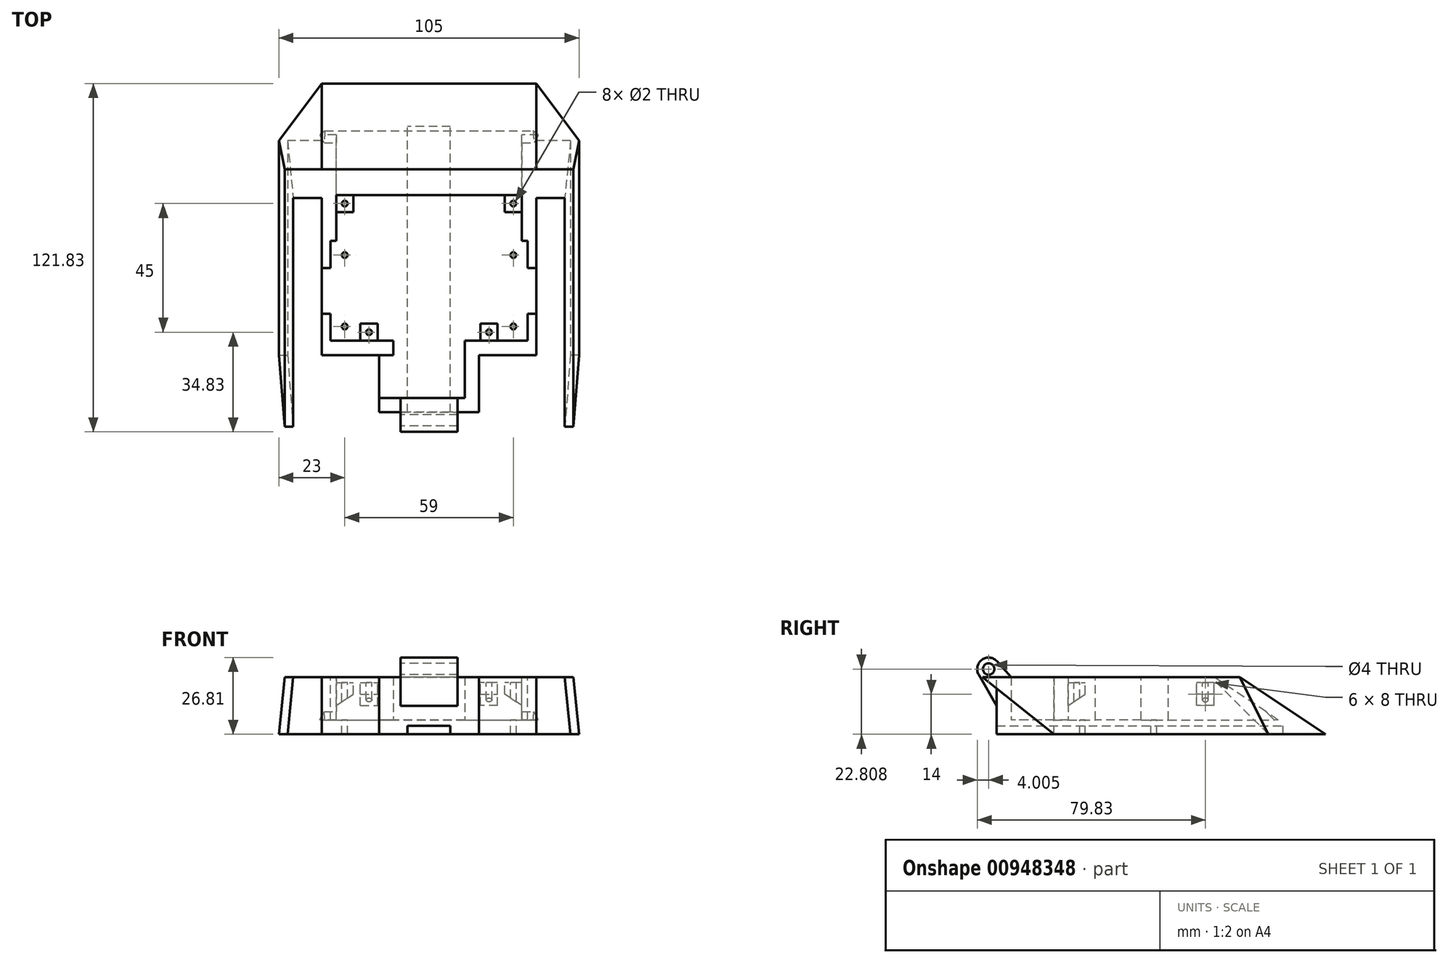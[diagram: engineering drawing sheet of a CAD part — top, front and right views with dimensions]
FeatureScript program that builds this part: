
annotation { "Feature Type Name" : "Feature", "Feature Type Description" : "" }
export const myFeature = defineFeature(function(context is Context, id is Id, definition is map)
    precondition{}
    {
        {
            var Q0;
            Q0=qCreatedBy(makeId("Top.planeOp"),FACE);
            var sketch = newSketch(context, id + "F0", { "sketchPlane" : qUnion([Q0])});
            skLineSegment(sketch, "E0.bottom", {"start": v(-37.5, -37.5) * mm, "end": v(37.5, -37.5) * mm});
            skLineSegment(sketch, "E0.top", {"start": v(-37.5, 37.5) * mm, "end": v(37.5, 37.5) * mm, "construction": true});
            skLineSegment(sketch, "E0.left", {"start": v(-37.5, -37.5) * mm, "end": v(-37.5, 37.5) * mm});
            skLineSegment(sketch, "E0.right", {"start": v(37.5, -37.5) * mm, "end": v(37.5, 37.5) * mm});
            skPoint(sketch, "E0.middle", {"position": v(0, 0) * mm});
            skLineSegment(sketch, "E1", {"start": v(-37.5, 37.5) * mm, "end": v(-49.5, 37.5) * mm});
            skLineSegment(sketch, "E2", {"start": v(-52.5, 37.5) * mm, "end": v(-37.5, 57.5) * mm});
            skLineSegment(sketch, "E3", {"start": v(-37.5, 57.5) * mm, "end": v(37.5, 57.5) * mm});
            skLineSegment(sketch, "E4", {"start": v(37.5, 57.5) * mm, "end": v(52.5, 37.5) * mm});
            skLineSegment(sketch, "E5", {"start": v(52.5, 37.5) * mm, "end": v(37.5, 37.5) * mm});
            skLineSegment(sketch, "E6.bottom", {"start": v(-52.5, 37.5) * mm, "end": v(-49.5, 37.5) * mm, "construction": true});
            skLineSegment(sketch, "E6.top", {"start": v(-52.5, -37.5) * mm, "end": v(-49.5, -37.5) * mm});
            skLineSegment(sketch, "E6.left", {"start": v(-52.5, 37.5) * mm, "end": v(-52.5, 21.64) * mm});
            skLineSegment(sketch, "E7.bottom", {"start": v(52.5, 37.5) * mm, "end": v(49.5, 37.5) * mm, "construction": true});
            skLineSegment(sketch, "E7.top", {"start": v(52.5, -37.5) * mm, "end": v(49.5, -37.5) * mm});
            skLineSegment(sketch, "E7.left", {"start": v(52.5, 37.5) * mm, "end": v(52.5, 21.33) * mm});
            skLineSegment(sketch, "E8", {"start": v(-52.5, 21.64) * mm, "end": v(-52.5, -37.5) * mm});
            skLineSegment(sketch, "E9", {"start": v(52.5, 21.33) * mm, "end": v(52.5, -37.5) * mm});
            skLineSegment(sketch, "E10", {"start": v(-49.5, 37.5) * mm, "end": v(-49.5, -37.5) * mm});
            skLineSegment(sketch, "E11", {"start": v(49.5, 37.5) * mm, "end": v(49.5, -37.5) * mm});
            skLineSegment(sketch, "E12", {"start": v(17.5, -37.5) * mm, "end": v(17.5, -57.5) * mm});
            skLineSegment(sketch, "E13", {"start": v(17.5, -57.5) * mm, "end": v(-17.5, -57.5) * mm});
            skLineSegment(sketch, "E14", {"start": v(-17.5, -57.5) * mm, "end": v(-17.5, -37.5) * mm});
            skSolve(sketch);
        }
        {
            var Q0;
            Q0=makeQuery(id+"F0.imprint","IMPRINT",FACE,{"disambiguationData":[TD([[makeQuery(id+"F0.imprint","IMPRINT",EDGE,{"derivedFrom":sQuery(id+"F0.wireOp",EDGE,"E0.bottom")}),1.0]])]});
            cPlane(context, id + "F1", {"entities" : qUnion([Q0]), "cplaneType" : CPlaneType.OFFSET, "offset" : 20 * mm, "width" : 150 * mm, "height" : 150 * mm});
        }
        {
            var Q0;
            Q0=qCreatedBy(id+"F1.planeOp",FACE);
            var sketch = newSketch(context, id + "F2", { "sketchPlane" : qUnion([Q0])});
            skLineSegment(sketch, "E15.bottom", {"start": v(-37.5, 27.5) * mm, "end": v(37.5, 27.5) * mm});
            skLineSegment(sketch, "E15.top", {"start": v(-37.5, -37.5) * mm, "end": v(37.5, -37.5) * mm});
            skLineSegment(sketch, "E15.left", {"start": v(-37.5, 17.5) * mm, "end": v(-37.5, -37.5) * mm});
            skLineSegment(sketch, "E15.right", {"start": v(37.5, 17.5) * mm, "end": v(37.5, -37.5) * mm});
            skPoint(sketch, "E15.middle", {"position": v(0, -5) * mm});
            skLineSegment(sketch, "E16.bottom", {"start": v(-37.5, 27.5) * mm, "end": v(-50.5, 27.5) * mm});
            skLineSegment(sketch, "E16.top", {"start": v(-37.5, 17.5) * mm, "end": v(-47.5, 17.5) * mm});
            skLineSegment(sketch, "E16.right", {"start": v(-50.5, 27.5) * mm, "end": v(-50.5, 17.5) * mm});
            skLineSegment(sketch, "E17.bottom", {"start": v(37.5, 27.5) * mm, "end": v(50.5, 27.5) * mm});
            skLineSegment(sketch, "E17.top", {"start": v(37.5, 17.5) * mm, "end": v(47.5, 17.5) * mm});
            skLineSegment(sketch, "E17.right", {"start": v(50.5, 27.5) * mm, "end": v(50.5, 17.5) * mm});
            skLineSegment(sketch, "E18.top", {"start": v(-50.5, -62.5) * mm, "end": v(-47.5, -62.5) * mm});
            skLineSegment(sketch, "E18.left", {"start": v(-50.5, 17.5) * mm, "end": v(-50.5, -62.5) * mm});
            skLineSegment(sketch, "E18.right", {"start": v(-47.5, 17.5) * mm, "end": v(-47.5, -62.5) * mm});
            skLineSegment(sketch, "E19.top", {"start": v(50.5, -62.5) * mm, "end": v(47.5, -62.5) * mm});
            skLineSegment(sketch, "E19.left", {"start": v(50.5, 17.5) * mm, "end": v(50.5, -62.5) * mm});
            skLineSegment(sketch, "E19.right", {"start": v(47.5, 17.5) * mm, "end": v(47.5, -62.5) * mm});
            skLineSegment(sketch, "E20", {"start": v(17.5, -37.5) * mm, "end": v(17.5, -57.5) * mm});
            skLineSegment(sketch, "E21", {"start": v(17.5, -57.5) * mm, "end": v(-17.5, -57.5) * mm});
            skLineSegment(sketch, "E22", {"start": v(-17.5, -57.5) * mm, "end": v(-17.5, -37.5) * mm});
            skSolve(sketch);
        }
        {
            var Q0;
            Q0 = qSketchRegion(id + "F0", true);
            var Q1;
            Q1 = qSketchRegion(id + "F2", true);
            loft(context, id + "F3", {"sheetProfilesArray" : [{ "sheetProfileEntities" : qUnion([Q0]) }, { "sheetProfileEntities" : qUnion([Q1]) }]});
        }
        {
            var Q0;
            Q0=makeQuery(id+"F3.opLoft","CAP_FACE",FACE,{"disambiguationData":[OSD([makeQuery(id+"F2.imprint","IMPRINT",FACE,{"disambiguationData":[TD([[makeQuery(id+"F2.imprint","IMPRINT",EDGE,{"derivedFrom":sQuery(id+"F2.wireOp",EDGE,"E15.bottom")}),-1.0]])]})])],"isStart":true});
            shell(context, id + "F4", {"entities" : qUnion([Q0]), "thickness" : 5 * mm});
        }
        {
            var Q0;
            Q0=makeQuery(id+"F3.opLoft","CAP_FACE",FACE,{"disambiguationData":[OSD([makeQuery(id+"F2.imprint","IMPRINT",FACE,{"disambiguationData":[TD([[makeQuery(id+"F2.imprint","IMPRINT",EDGE,{"derivedFrom":sQuery(id+"F2.wireOp",EDGE,"E15.bottom")}),-1.0]])]})])],"isStart":true});
            var sketch = newSketch(context, id + "F5", { "sketchPlane" : qUnion([Q0])});
            skLineSegment(sketch, "E23", {"start": v(-32.5, -32.5) * mm, "end": v(-34.5, -32.5) * mm});
            skLineSegment(sketch, "E24", {"start": v(-34.5, -32.5) * mm, "end": v(-34.5, -23) * mm});
            skLineSegment(sketch, "E25", {"start": v(-34.5, -23) * mm, "end": v(-37.5, -23) * mm});
            skLineSegment(sketch, "E26", {"start": v(-37.5, -23) * mm, "end": v(-37.5, -7) * mm});
            skLineSegment(sketch, "E27", {"start": v(-37.5, -7) * mm, "end": v(-34.5, -7) * mm});
            skLineSegment(sketch, "E28", {"start": v(-34.5, -7) * mm, "end": v(-34.5, 2.5) * mm});
            skLineSegment(sketch, "E29", {"start": v(-34.5, 2.5) * mm, "end": v(-32.5, 2.5) * mm});
            skLineSegment(sketch, "E30", {"start": v(32.5, -32.5) * mm, "end": v(32.5, -32.5) * mm});
            skLineSegment(sketch, "E31", {"start": v(32.5, -32.5) * mm, "end": v(34.5, -32.5) * mm});
            skLineSegment(sketch, "E32", {"start": v(34.5, -32.5) * mm, "end": v(34.5, -23) * mm});
            skLineSegment(sketch, "E33", {"start": v(34.5, -23) * mm, "end": v(37.5, -23) * mm});
            skLineSegment(sketch, "E34", {"start": v(37.5, -23) * mm, "end": v(37.5, -7) * mm});
            skLineSegment(sketch, "E35", {"start": v(37.5, -7) * mm, "end": v(34.5, -7) * mm});
            skLineSegment(sketch, "E36", {"start": v(34.5, -7) * mm, "end": v(34.5, 2.5) * mm});
            skLineSegment(sketch, "E37", {"start": v(34.5, 2.5) * mm, "end": v(32.5, 2.5) * mm});
            skSolve(sketch);
        }
        {
            var Q0;
            {var subQ0=sQuery(id+"F5.wireOp",EDGE,"E31");Q0=makeQuery(id+"F5.imprint","IMPRINT",FACE,{"disambiguationData":[TD([[makeQuery(id+"F5.imprint","IMPRINT",EDGE,{"derivedFrom":subQ0}),1.0]])]});}
            var Q1;
            {var subQ0=sQuery(id+"F5.wireOp",EDGE,"E23");Q1=makeQuery(id+"F5.imprint","IMPRINT",FACE,{"disambiguationData":[TD([[makeQuery(id+"F5.imprint","IMPRINT",EDGE,{"derivedFrom":subQ0}),-1.0]])]});}
            extrude(context, id + "F6", {"entities" : qUnion([Q0, Q1]), "operationType" : NewBodyOperationType.REMOVE, "oppositeDirection" : true, "depth" : 15 * mm, "offsetDistance" : 25 * mm});
        }
        {
            var Q0;
            {var subQ0=sQuery(id+"F2.wireOp",EDGE,"E15.top");Q0=makeQuery(id+"F6.boolean.opBoolean","MERGE",FACE,{"derivedFrom":[makeQuery(id+"F4.opShell","OFFSET_FACE",FACE,{"disambiguationData":[OSD([makeQuery(id+"F0.imprint","IMPRINT",FACE,{"disambiguationData":[TD([[makeQuery(id+"F0.imprint","IMPRINT",EDGE,{"derivedFrom":sQuery(id+"F0.wireOp",EDGE,"E0.bottom")}),1.0]])]}),makeQuery(id+"F0.imprint","IMPRINT",FACE,{"disambiguationData":[TD([[makeQuery(id+"F0.imprint","IMPRINT",EDGE,{"derivedFrom":sQuery(id+"F0.wireOp",EDGE,"E7.top")}),-1.0]])]})])]})],"fromTools":[makeQuery(id+"F6.opExtrude","CAP_FACE",FACE,{"disambiguationData":[OSD([subQ0,sQuery(id+"F2.wireOp",EDGE,"E15.left"),sQuery(id+"F2.wireOp",EDGE,"E16.top"),sQuery(id+"F5.wireOp",EDGE,"E23"),sQuery(id+"F5.wireOp",EDGE,"E24"),sQuery(id+"F5.wireOp",EDGE,"E25"),sQuery(id+"F5.wireOp",EDGE,"E26"),sQuery(id+"F5.wireOp",EDGE,"E27"),sQuery(id+"F5.wireOp",EDGE,"E28"),sQuery(id+"F5.wireOp",EDGE,"E29")])],"isStart":false}),makeQuery(id+"F6.opExtrude","CAP_FACE",FACE,{"disambiguationData":[OSD([subQ0,sQuery(id+"F2.wireOp",EDGE,"E15.right"),sQuery(id+"F2.wireOp",EDGE,"E17.top"),sQuery(id+"F5.wireOp",EDGE,"E31"),sQuery(id+"F5.wireOp",EDGE,"E32"),sQuery(id+"F5.wireOp",EDGE,"E33"),sQuery(id+"F5.wireOp",EDGE,"E34"),sQuery(id+"F5.wireOp",EDGE,"E35"),sQuery(id+"F5.wireOp",EDGE,"E36"),sQuery(id+"F5.wireOp",EDGE,"E37")])],"isStart":false})]});}
            var sketch = newSketch(context, id + "F7", { "sketchPlane" : qUnion([Q0])});
            skCircle(sketch, "E38", {"center": v(-29.5, -27.5) * mm, "radius": 1 * mm});
            skCircle(sketch, "E39", {"center": v(-29.5, -2.5) * mm, "radius": 1 * mm});
            skCircle(sketch, "E40", {"center": v(29.5, -27.5) * mm, "radius": 1 * mm});
            skCircle(sketch, "E41", {"center": v(29.5, -2.5) * mm, "radius": 1 * mm});
            skSolve(sketch);
        }
        {
            var Q0;
            Q0=makeQuery(id+"F7.imprint","IMPRINT",FACE,{"disambiguationData":[TD([[makeQuery(id+"F7.imprint","IMPRINT",EDGE,{"derivedFrom":sQuery(id+"F7.wireOp",EDGE,"E38")}),1.0]])]});
            var Q1;
            Q1=makeQuery(id+"F7.imprint","IMPRINT",FACE,{"disambiguationData":[TD([[makeQuery(id+"F7.imprint","IMPRINT",EDGE,{"derivedFrom":sQuery(id+"F7.wireOp",EDGE,"E41")}),1.0]])]});
            var Q2;
            Q2=makeQuery(id+"F7.imprint","IMPRINT",FACE,{"disambiguationData":[TD([[makeQuery(id+"F7.imprint","IMPRINT",EDGE,{"derivedFrom":sQuery(id+"F7.wireOp",EDGE,"E40")}),1.0]])]});
            var Q3;
            Q3=makeQuery(id+"F7.imprint","IMPRINT",FACE,{"disambiguationData":[TD([[makeQuery(id+"F7.imprint","IMPRINT",EDGE,{"derivedFrom":sQuery(id+"F7.wireOp",EDGE,"E39")}),1.0]])]});
            extrude(context, id + "F8", {"entities" : qUnion([Q0, Q1, Q2, Q3]), "operationType" : NewBodyOperationType.REMOVE, "oppositeDirection" : true, "depth" : 25 * mm, "offsetDistance" : 25 * mm});
        }
        {
            var Q0;
            {var subQ15=sQuery(id+"F2.wireOp",EDGE,"E15.bottom");Q0=makeQuery(id+"F6.boolean.opBoolean","SPLIT",FACE,{"disambiguationData":[TD([makeQuery(id+"F6.opExtrude","SWEPT_FACE",FACE,{"disambiguationData":[OSD([sQuery(id+"F5.wireOp",EDGE,"E27")])]})])],"derivedFrom":makeQuery(id+"F3.opLoft","CAP_FACE",FACE,{"disambiguationData":[OSD([makeQuery(id+"F2.imprint","IMPRINT",FACE,{"disambiguationData":[TD([[makeQuery(id+"F2.imprint","IMPRINT",EDGE,{"derivedFrom":subQ15}),-1.0]])]})])],"isStart":true})});}
            cPlane(context, id + "F9", {"entities" : qUnion([Q0]), "cplaneType" : CPlaneType.OFFSET, "offset" : 2 * mm, "oppositeDirection" : true, "width" : 150 * mm, "height" : 150 * mm});
        }
        {
            var Q0;
            Q0=qCreatedBy(id+"F9.planeOp",FACE);
            var sketch = newSketch(context, id + "F10", { "sketchPlane" : qUnion([Q0])});
            skLineSegment(sketch, "E42.bottom", {"start": v(32.5, 18.5) * mm, "end": v(26.5, 18.5) * mm});
            skLineSegment(sketch, "E42.top", {"start": v(32.5, 12.5) * mm, "end": v(26.5, 12.5) * mm});
            skLineSegment(sketch, "E42.left", {"start": v(32.5, 18.5) * mm, "end": v(32.5, 12.5) * mm});
            skLineSegment(sketch, "E42.right", {"start": v(26.5, 18.5) * mm, "end": v(26.5, 12.5) * mm});
            skCircle(sketch, "E43", {"center": v(29.5, 15.5) * mm, "radius": 1 * mm});
            skPoint(sketch, "E43.centerSnap0", {"position": v(29.5, 12.5) * mm});
            skPoint(sketch, "E43.centerSnap1", {"position": v(26.5, 15.5) * mm});
            skLineSegment(sketch, "E44.bottom", {"start": v(24, -32.5) * mm, "end": v(18, -32.5) * mm});
            skLineSegment(sketch, "E44.top", {"start": v(24, -26.5) * mm, "end": v(18, -26.5) * mm});
            skLineSegment(sketch, "E44.left", {"start": v(24, -32.5) * mm, "end": v(24, -26.5) * mm});
            skLineSegment(sketch, "E44.right", {"start": v(18, -32.5) * mm, "end": v(18, -26.5) * mm});
            skCircle(sketch, "E45", {"center": v(21, -29.5) * mm, "radius": 1 * mm});
            skPoint(sketch, "E45.centerSnap0", {"position": v(21, -26.5) * mm});
            skPoint(sketch, "E45.centerSnap1", {"position": v(18, -29.5) * mm});
            skLineSegment(sketch, "E46", {"start": v(0, 0) * mm, "end": v(0, -25.62) * mm});
            skLineSegment(sketch, "E47.MirrorCS", {"start": v(-24, -32.5) * mm, "end": v(-24, -26.5) * mm});
            skLineSegment(sketch, "E48.MirrorCS", {"start": v(-24, -26.5) * mm, "end": v(-18, -26.5) * mm});
            skLineSegment(sketch, "E49.MirrorCS", {"start": v(-18, -32.5) * mm, "end": v(-18, -26.5) * mm});
            skLineSegment(sketch, "E50.MirrorCS", {"start": v(-24, -32.5) * mm, "end": v(-18, -32.5) * mm});
            skCircle(sketch, "E51.MirrorC", {"center": v(-21, -29.5) * mm, "radius": 1 * mm});
            skLineSegment(sketch, "E52.MirrorCS", {"start": v(-32.5, 12.5) * mm, "end": v(-26.5, 12.5) * mm});
            skLineSegment(sketch, "E53.MirrorCS", {"start": v(-32.5, 18.5) * mm, "end": v(-32.5, 12.5) * mm});
            skLineSegment(sketch, "E54.MirrorCS", {"start": v(-32.5, 18.5) * mm, "end": v(-26.5, 18.5) * mm});
            skLineSegment(sketch, "E55.MirrorCS", {"start": v(-26.5, 18.5) * mm, "end": v(-26.5, 12.5) * mm});
            skCircle(sketch, "E56.MirrorC", {"center": v(-29.5, 15.5) * mm, "radius": 1 * mm});
            skSolve(sketch);
        }
        {
            var Q0;
            Q0=makeQuery(id+"F10.imprint","IMPRINT",FACE,{"disambiguationData":[TD([[makeQuery(id+"F10.imprint","IMPRINT",EDGE,{"derivedFrom":sQuery(id+"F10.wireOp",EDGE,"E47.MirrorCS")}),-1.0]])]});
            var Q1;
            Q1=makeQuery(id+"F10.imprint","IMPRINT",FACE,{"disambiguationData":[TD([[makeQuery(id+"F10.imprint","IMPRINT",EDGE,{"derivedFrom":sQuery(id+"F10.wireOp",EDGE,"E52.MirrorCS")}),1.0]])]});
            var Q2;
            Q2=makeQuery(id+"F10.imprint","IMPRINT",FACE,{"disambiguationData":[TD([[makeQuery(id+"F10.imprint","IMPRINT",EDGE,{"derivedFrom":sQuery(id+"F10.wireOp",EDGE,"E42.bottom")}),1.0]])]});
            var Q3;
            Q3=makeQuery(id+"F10.imprint","IMPRINT",FACE,{"disambiguationData":[TD([[makeQuery(id+"F10.imprint","IMPRINT",EDGE,{"derivedFrom":sQuery(id+"F10.wireOp",EDGE,"E44.bottom")}),-1.0]])]});
            extrude(context, id + "F11", {"entities" : qUnion([Q0, Q1, Q2, Q3]), "operationType" : NewBodyOperationType.ADD, "oppositeDirection" : true, "depth" : 8 * mm, "offsetDistance" : 25 * mm});
        }
        {
            var Q0;
            Q0=makeQuery(id+"F11.opExtrude","SWEPT_FACE",FACE,{"disambiguationData":[OSD([sQuery(id+"F10.wireOp",EDGE,"E42.top")])]});
            var sketch = newSketch(context, id + "F12", { "sketchPlane" : qUnion([Q0])});
            skLineSegment(sketch, "E57", {"start": v(32.5, 10) * mm, "end": v(26.5, 14) * mm});
            skSolve(sketch);
        }
        {
            var Q0;
            {var subQ0=sQuery(id+"F12.wireOp",EDGE,"E57");Q0=makeQuery(id+"F12.imprint","IMPRINT",FACE,{"disambiguationData":[TD([[makeQuery(id+"F12.imprint","IMPRINT",EDGE,{"derivedFrom":subQ0}),1.0]])]});}
            extrude(context, id + "F13", {"entities" : qUnion([Q0]), "operationType" : NewBodyOperationType.REMOVE, "oppositeDirection" : true, "depth" : 7 * mm, "offsetDistance" : 25 * mm});
        }
        {
            var Q0;
            Q0=makeQuery(id+"F11.opExtrude","SWEPT_FACE",FACE,{"disambiguationData":[OSD([sQuery(id+"F10.wireOp",EDGE,"E52.MirrorCS")])]});
            var sketch = newSketch(context, id + "F14", { "sketchPlane" : qUnion([Q0])});
            skLineSegment(sketch, "E58", {"start": v(-32.5, 10) * mm, "end": v(-26.5, 14) * mm});
            skSolve(sketch);
        }
        {
            var Q0;
            {var subQ0=sQuery(id+"F14.wireOp",EDGE,"E58");Q0=makeQuery(id+"F14.imprint","IMPRINT",FACE,{"disambiguationData":[TD([[makeQuery(id+"F14.imprint","IMPRINT",EDGE,{"derivedFrom":subQ0}),-1.0]])]});}
            extrude(context, id + "F15", {"entities" : qUnion([Q0]), "operationType" : NewBodyOperationType.REMOVE, "oppositeDirection" : true, "depth" : 7 * mm, "offsetDistance" : 25 * mm});
        }
        {
            var Q0;
            Q0=makeQuery(id+"F11.opExtrude","SWEPT_FACE",FACE,{"disambiguationData":[OSD([sQuery(id+"F10.wireOp",EDGE,"E44.left")])]});
            var sketch = newSketch(context, id + "F16", { "sketchPlane" : qUnion([Q0])});
            skLineSegment(sketch, "E59", {"start": v(-32.5, 10) * mm, "end": v(-26.5, 14) * mm});
            skSolve(sketch);
        }
        {
            var Q0;
            {var subQ0=sQuery(id+"F16.wireOp",EDGE,"E59");Q0=makeQuery(id+"F16.imprint","IMPRINT",FACE,{"disambiguationData":[TD([[makeQuery(id+"F16.imprint","IMPRINT",EDGE,{"derivedFrom":subQ0}),-1.0]])]});}
            extrude(context, id + "F17", {"entities" : qUnion([Q0]), "operationType" : NewBodyOperationType.REMOVE, "oppositeDirection" : true, "depth" : 50 * mm, "offsetDistance" : 25 * mm});
        }
        {
            var Q0;
            Q0=makeQuery(id+"F3.opLoft","SWEPT_FACE",FACE,{"disambiguationData":[OSD([sQuery(id+"F0.wireOp",EDGE,"E0.bottom"),sQuery(id+"F0.wireOp",EDGE,"E13"),sQuery(id+"F0.wireOp",EDGE,"E14"),sQuery(id+"F2.wireOp",EDGE,"E15.top"),sQuery(id+"F2.wireOp",EDGE,"E21"),sQuery(id+"F2.wireOp",EDGE,"E22")])]});
            var sketch = newSketch(context, id + "F18", { "sketchPlane" : qUnion([Q0])});
            skLineSegment(sketch, "E60.bottom", {"start": v(37.5, 20) * mm, "end": v(52.5, 20) * mm});
            skLineSegment(sketch, "E60.top", {"start": v(37.5, 5) * mm, "end": v(52.5, 5) * mm});
            skLineSegment(sketch, "E60.left", {"start": v(37.5, 20) * mm, "end": v(37.5, 5) * mm});
            skLineSegment(sketch, "E60.right", {"start": v(52.5, 20) * mm, "end": v(52.5, 5) * mm});
            skSolve(sketch);
        }
        {
            var Q0;
            Q0=makeQuery(id+"F18.imprint","IMPRINT",FACE,{"disambiguationData":[TD([[makeQuery(id+"F18.imprint","IMPRINT",EDGE,{"derivedFrom":sQuery(id+"F18.wireOp",EDGE,"E60.bottom")}),-1.0]])]});
            extrude(context, id + "F19", {"entities" : qUnion([Q0]), "operationType" : NewBodyOperationType.REMOVE, "oppositeDirection" : true, "depth" : 25 * mm, "offsetDistance" : 25 * mm});
        }
        {
            var Q0;
            Q0=makeQuery(id+"F3.opLoft","SWEPT_FACE",FACE,{"disambiguationData":[OSD([sQuery(id+"F0.wireOp",EDGE,"E0.bottom"),sQuery(id+"F0.wireOp",EDGE,"E12"),sQuery(id+"F0.wireOp",EDGE,"E13"),sQuery(id+"F2.wireOp",EDGE,"E15.top"),sQuery(id+"F2.wireOp",EDGE,"E20"),sQuery(id+"F2.wireOp",EDGE,"E21")])]});
            cPlane(context, id + "F20", {"entities" : qUnion([Q0]), "cplaneType" : CPlaneType.OFFSET, "offset" : 17.5 * mm, "oppositeDirection" : true, "width" : 150 * mm, "height" : 150 * mm});
        }
        {
            var Q0;
            Q0=qCreatedBy(id+"F20.planeOp",FACE);
            var sketch = newSketch(context, id + "F21", { "sketchPlane" : qUnion([Q0])});
            skPoint(sketch, "E61", {"position": v(-57.5, 19.98) * mm});
            skLineSegment(sketch, "E62", {"start": v(-57.5, 19.98) * mm, "end": v(-63.15, 19.98) * mm});
            skLineSegment(sketch, "E63", {"start": v(-57.5, 19.98) * mm, "end": v(-63.42, 25.9) * mm});
            skCircle(sketch, "E64", {"center": v(-60.33, 22.8) * mm, "radius": 4 * mm});
            skPoint(sketch, "E64.centerSnap0", {"position": v(-60.33, 19.98) * mm});
            skCircle(sketch, "E65", {"center": v(-60.33, 22.8) * mm, "radius": 2 * mm});
            skLineSegment(sketch, "E66", {"start": v(-57.5, 19.98) * mm, "end": v(-52.5, 19.98) * mm});
            skLineSegment(sketch, "E67", {"start": v(-57.5, 19.98) * mm, "end": v(-57.5, 9.98) * mm});
            skLineSegment(sketch, "E68", {"start": v(-57.5, 9.98) * mm, "end": v(-63.78, 20.8) * mm});
            skLineSegment(sketch, "E69", {"start": v(-52.5, 19.98) * mm, "end": v(-57.33, 25.45) * mm});
            skSolve(sketch);
        }
        {
            var Q0;
            {var subQ0=sQuery(id+"F21.wireOp",EDGE,"E62");Q0=makeQuery(id+"F21.imprint","IMPRINT",FACE,{"disambiguationData":[TD([[makeQuery(id+"F21.imprint","IMPRINT",EDGE,{"derivedFrom":subQ0}),1.0]])]});}
            var Q1;
            {var subQ5=sQuery(id+"F21.wireOp",EDGE,"E62");Q1=makeQuery(id+"F21.imprint","IMPRINT",FACE,{"disambiguationData":[TD([[makeQuery(id+"F21.imprint","IMPRINT",EDGE,{"derivedFrom":subQ5}),-1.0]])]});}
            var Q2;
            {var subQ0=sQuery(id+"F21.wireOp",EDGE,"E66");Q2=makeQuery(id+"F21.imprint","IMPRINT",FACE,{"disambiguationData":[TD([[makeQuery(id+"F21.imprint","IMPRINT",EDGE,{"derivedFrom":subQ0}),1.0]])]});}
            var Q3;
            {var subQ0=sQuery(id+"F21.wireOp",EDGE,"E64");var subQ2=sQuery(id+"F21.wireOp",EDGE,"E63");var subQ3=makeQuery(id+"F21.imprint","INTERSECT",VERTEX,{"derivedFrom":[subQ2,subQ0]});Q3=makeQuery(id+"F21.imprint","IMPRINT",FACE,{"disambiguationData":[TD([[makeQuery(id+"F21.imprint","IMPRINT",EDGE,{"disambiguationData":[TD([[subQ3,1.0]])],"derivedFrom":subQ2}),-1.0]])]});}
            var Q4;
            {var subQ4=sQuery(id+"F21.wireOp",EDGE,"E67");Q4=makeQuery(id+"F21.imprint","IMPRINT",FACE,{"disambiguationData":[TD([[makeQuery(id+"F21.imprint","IMPRINT",EDGE,{"derivedFrom":subQ4}),-1.0]])]});}
            extrude(context, id + "F22", {"entities" : qUnion([Q0, Q1, Q2, Q3, Q4]), "operationType" : NewBodyOperationType.ADD, "endBound" : BoundingType.SYMMETRIC, "depth" : 20 * mm, "offsetDistance" : 25 * mm});
        }
        {
            var Q0;
            {var subQ7=sQuery(id+"F0.wireOp",EDGE,"E0.left");var subQ11=sQuery(id+"F0.wireOp",EDGE,"E12");Q0=makeQuery(id+"F3.opLoft","CAP_FACE",FACE,{"disambiguationData":[OSD([makeQuery(id+"F0.imprint","IMPRINT",FACE,{"disambiguationData":[TD([[makeQuery(id+"F0.imprint","IMPRINT",EDGE,{"derivedFrom":subQ11}),-1.0]])]}),makeQuery(id+"F0.imprint","IMPRINT",FACE,{"disambiguationData":[TD([[makeQuery(id+"F0.imprint","IMPRINT",EDGE,{"derivedFrom":sQuery(id+"F0.wireOp",EDGE,"E7.top")}),-1.0]])]}),makeQuery(id+"F0.imprint","IMPRINT",FACE,{"disambiguationData":[TD([[makeQuery(id+"F0.imprint","IMPRINT",EDGE,{"derivedFrom":subQ7}),-1.0]])]})])],"isStart":true});}
            var sketch = newSketch(context, id + "F23", { "sketchPlane" : qUnion([Q0])});
            skLineSegment(sketch, "E70.bottom", {"start": v(7.5, 57.5) * mm, "end": v(-7.5, 57.5) * mm});
            skLineSegment(sketch, "E70.top", {"start": v(7.5, -42.5) * mm, "end": v(-7.5, -42.5) * mm});
            skLineSegment(sketch, "E70.left", {"start": v(7.5, 57.5) * mm, "end": v(7.5, -42.5) * mm});
            skLineSegment(sketch, "E70.right", {"start": v(-7.5, 57.5) * mm, "end": v(-7.5, -42.5) * mm});
            skSolve(sketch);
        }
        {
            var Q0;
            Q0=makeQuery(id+"F23.imprint","IMPRINT",FACE,{"disambiguationData":[TD([[makeQuery(id+"F23.imprint","IMPRINT",EDGE,{"derivedFrom":sQuery(id+"F23.wireOp",EDGE,"E70.bottom")}),-1.0]])]});
            extrude(context, id + "F24", {"entities" : qUnion([Q0]), "operationType" : NewBodyOperationType.REMOVE, "oppositeDirection" : true, "depth" : 3 * mm, "offsetDistance" : 25 * mm});
        }
    });
